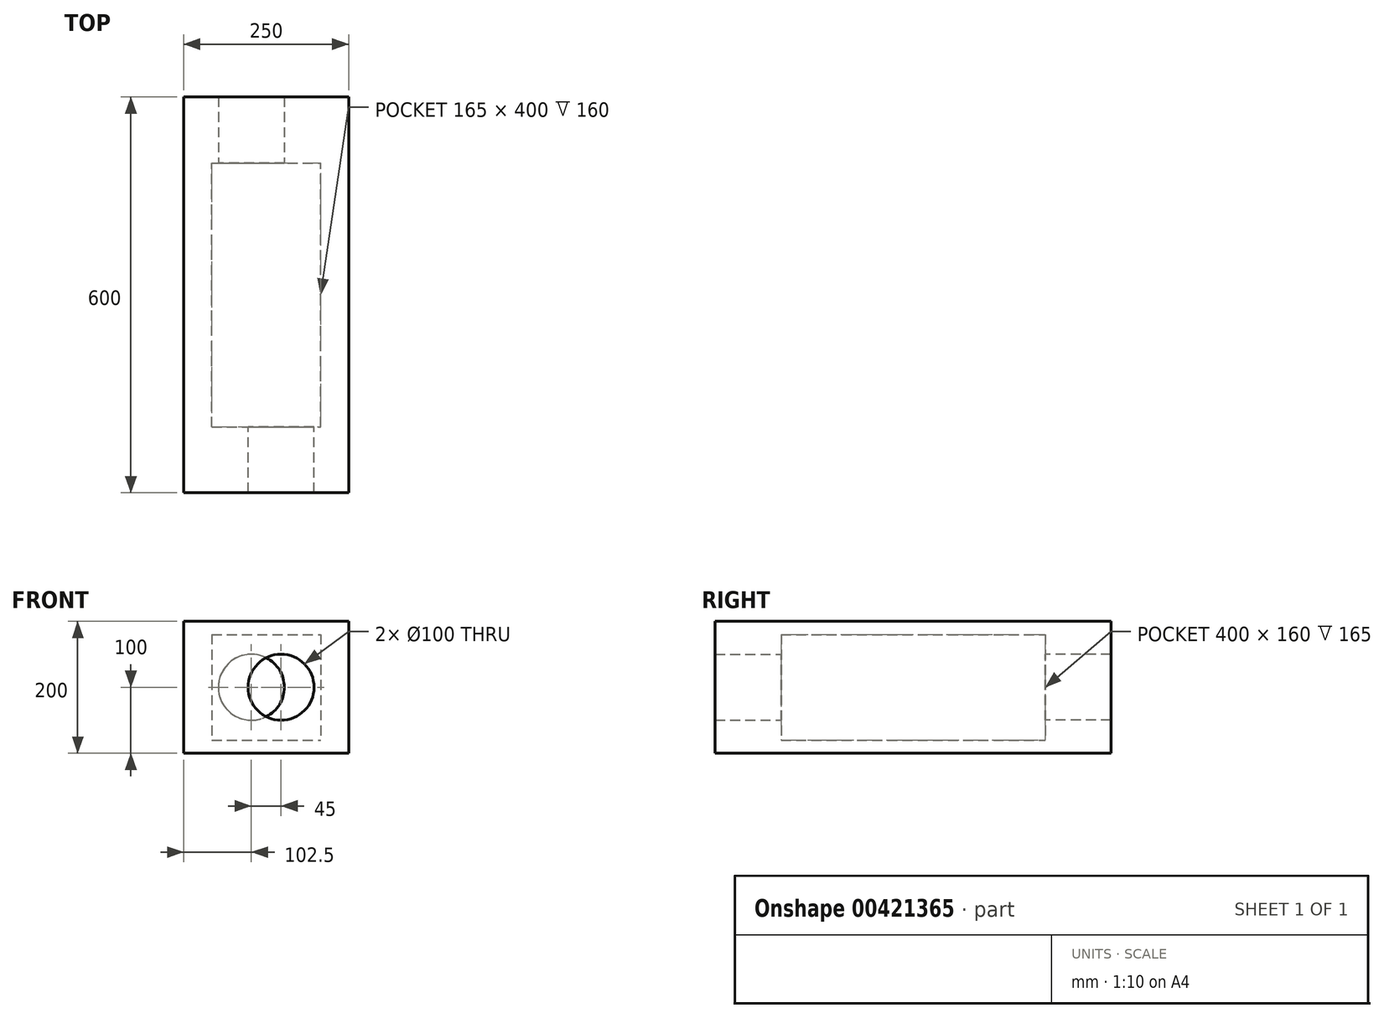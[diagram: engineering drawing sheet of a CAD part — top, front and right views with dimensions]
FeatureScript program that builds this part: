
annotation { "Feature Type Name" : "Feature", "Feature Type Description" : "" }
export const myFeature = defineFeature(function(context is Context, id is Id, definition is map)
    precondition{}
    {
        {
            var Q0;
            Q0=qCreatedBy(makeId("Front.planeOp"),FACE);
            var sketch = newSketch(context, id + "F0", { "sketchPlane" : qUnion([Q0])});
            skCircle(sketch, "E0", {"center": v(0, 0) * mm, "radius": 50 * mm});
            skCircle(sketch, "E1", {"center": v(45, 0) * mm, "radius": 50 * mm});
            skLineSegment(sketch, "E2", {"start": v(0, 0) * mm, "end": v(45, 0) * mm, "construction": true});
            skLineSegment(sketch, "E3.bottom", {"start": v(147.5, 100) * mm, "end": v(-102.5, 100) * mm});
            skLineSegment(sketch, "E3.top", {"start": v(147.5, -100) * mm, "end": v(-102.5, -100) * mm});
            skLineSegment(sketch, "E3.left", {"start": v(147.5, 100) * mm, "end": v(147.5, -100) * mm});
            skLineSegment(sketch, "E3.right", {"start": v(-102.5, 100) * mm, "end": v(-102.5, -100) * mm});
            skPoint(sketch, "E3.middle", {"position": v(22.5, 0) * mm});
            skLineSegment(sketch, "E4.bottom", {"start": v(95, 50) * mm, "end": v(-50, 50) * mm, "construction": true});
            skLineSegment(sketch, "E4.top", {"start": v(95, -50) * mm, "end": v(-50, -50) * mm, "construction": true});
            skLineSegment(sketch, "E4.left", {"start": v(95, 50) * mm, "end": v(95, -50) * mm, "construction": true});
            skLineSegment(sketch, "E4.right", {"start": v(-50, 50) * mm, "end": v(-50, -50) * mm, "construction": true});
            skLineSegment(sketch, "E5.1", {"start": v(105, 80) * mm, "end": v(105, -80) * mm});
            skLineSegment(sketch, "E5.3", {"start": v(-60, 80) * mm, "end": v(-60, -80) * mm});
            skPoint(sketch, "E6", {"position": v(-60, 0) * mm});
            skPoint(sketch, "E7", {"position": v(105, 0) * mm});
            skLineSegment(sketch, "E8", {"start": v(-60, 0) * mm, "end": v(-50, 0) * mm, "construction": true});
            skLineSegment(sketch, "E9", {"start": v(105, 0) * mm, "end": v(95, 0) * mm, "construction": true});
            skLineSegment(sketch, "E10", {"start": v(-60, 80) * mm, "end": v(105, 80) * mm});
            skLineSegment(sketch, "E11", {"start": v(-60, -80) * mm, "end": v(105, -80) * mm});
            skSolve(sketch);
        }
        {
            var Q0;
            Q0=makeQuery(id+"F0.imprint","IMPRINT",FACE,{"disambiguationData":[TD([[makeQuery(id+"F0.imprint","IMPRINT",EDGE,{"derivedFrom":sQuery(id+"F0.wireOp",EDGE,"E3.bottom")}),1.0]])]});
            var Q1;
            Q1=makeQuery(id+"F0.imprint","IMPRINT",FACE,{"disambiguationData":[TD([[makeQuery(id+"F0.imprint","IMPRINT",EDGE,{"derivedFrom":sQuery(id+"F0.wireOp",EDGE,"E5.1")}),-1.0]])]});
            var Q2;
            {var subQ0=sQuery(id+"F0.wireOp",EDGE,"E1");var subQ1=sQuery(id+"F0.wireOp",EDGE,"E0");var subQ2=makeQuery(id+"F0.imprint","INTERSECT",VERTEX,{"disambiguationData":[OD(0.0)],"derivedFrom":[subQ1,subQ0]});Q2=makeQuery(id+"F0.imprint","IMPRINT",FACE,{"disambiguationData":[TD([[makeQuery(id+"F0.imprint","IMPRINT",EDGE,{"disambiguationData":[TD([[subQ2,1.0]])],"derivedFrom":subQ1}),1.0]])]});}
            var Q3;
            {var subQ0=sQuery(id+"F0.wireOp",EDGE,"E1");var subQ1=sQuery(id+"F0.wireOp",EDGE,"E0");var subQ2=makeQuery(id+"F0.imprint","INTERSECT",VERTEX,{"disambiguationData":[OD(0.0)],"derivedFrom":[subQ1,subQ0]});Q3=makeQuery(id+"F0.imprint","IMPRINT",FACE,{"disambiguationData":[TD([[makeQuery(id+"F0.imprint","IMPRINT",EDGE,{"disambiguationData":[TD([[subQ2,-1.0]])],"derivedFrom":subQ1}),1.0]])]});}
            var Q4;
            {var subQ0=sQuery(id+"F0.wireOp",EDGE,"E1");var subQ1=sQuery(id+"F0.wireOp",EDGE,"E0");var subQ2=makeQuery(id+"F0.imprint","INTERSECT",VERTEX,{"disambiguationData":[OD(0.0)],"derivedFrom":[subQ1,subQ0]});Q4=makeQuery(id+"F0.imprint","IMPRINT",FACE,{"disambiguationData":[TD([[makeQuery(id+"F0.imprint","IMPRINT",EDGE,{"disambiguationData":[TD([[subQ2,-1.0]])],"derivedFrom":subQ1}),-1.0]])]});}
            extrude(context, id + "F1", {"entities" : qUnion([Q0, Q1, Q2, Q3, Q4]), "depth" : 300 * mm, "hasSecondDirection" : true, "secondDirectionOppositeDirection" : true, "secondDirectionDepth" : 300 * mm});
        }
        {
            var Q0;
            Q0=makeQuery(id+"F0.imprint","IMPRINT",FACE,{"disambiguationData":[TD([[makeQuery(id+"F0.imprint","IMPRINT",EDGE,{"derivedFrom":sQuery(id+"F0.wireOp",EDGE,"E5.1")}),-1.0]])]});
            var Q1;
            {var subQ0=sQuery(id+"F0.wireOp",EDGE,"E1");var subQ1=sQuery(id+"F0.wireOp",EDGE,"E0");var subQ2=makeQuery(id+"F0.imprint","INTERSECT",VERTEX,{"disambiguationData":[OD(0.0)],"derivedFrom":[subQ1,subQ0]});Q1=makeQuery(id+"F0.imprint","IMPRINT",FACE,{"disambiguationData":[TD([[makeQuery(id+"F0.imprint","IMPRINT",EDGE,{"disambiguationData":[TD([[subQ2,1.0]])],"derivedFrom":subQ1}),1.0]])]});}
            var Q2;
            {var subQ0=sQuery(id+"F0.wireOp",EDGE,"E1");var subQ1=sQuery(id+"F0.wireOp",EDGE,"E0");var subQ2=makeQuery(id+"F0.imprint","INTERSECT",VERTEX,{"disambiguationData":[OD(0.0)],"derivedFrom":[subQ1,subQ0]});Q2=makeQuery(id+"F0.imprint","IMPRINT",FACE,{"disambiguationData":[TD([[makeQuery(id+"F0.imprint","IMPRINT",EDGE,{"disambiguationData":[TD([[subQ2,-1.0]])],"derivedFrom":subQ1}),1.0]])]});}
            var Q3;
            {var subQ0=sQuery(id+"F0.wireOp",EDGE,"E1");var subQ1=sQuery(id+"F0.wireOp",EDGE,"E0");var subQ2=makeQuery(id+"F0.imprint","INTERSECT",VERTEX,{"disambiguationData":[OD(0.0)],"derivedFrom":[subQ1,subQ0]});Q3=makeQuery(id+"F0.imprint","IMPRINT",FACE,{"disambiguationData":[TD([[makeQuery(id+"F0.imprint","IMPRINT",EDGE,{"disambiguationData":[TD([[subQ2,-1.0]])],"derivedFrom":subQ1}),-1.0]])]});}
            extrude(context, id + "F2", {"entities" : qUnion([Q0, Q1, Q2, Q3]), "operationType" : NewBodyOperationType.REMOVE, "depth" : 200 * mm, "hasSecondDirection" : true, "secondDirectionOppositeDirection" : true, "secondDirectionDepth" : 200 * mm});
        }
        {
            var Q0;
            {var subQ0=sQuery(id+"F0.wireOp",EDGE,"E1");var subQ1=sQuery(id+"F0.wireOp",EDGE,"E0");var subQ2=makeQuery(id+"F0.imprint","INTERSECT",VERTEX,{"disambiguationData":[OD(0.0)],"derivedFrom":[subQ1,subQ0]});Q0=makeQuery(id+"F0.imprint","IMPRINT",FACE,{"disambiguationData":[TD([[makeQuery(id+"F0.imprint","IMPRINT",EDGE,{"disambiguationData":[TD([[subQ2,-1.0]])],"derivedFrom":subQ1}),1.0]])]});}
            var Q1;
            {var subQ0=sQuery(id+"F0.wireOp",EDGE,"E1");var subQ1=sQuery(id+"F0.wireOp",EDGE,"E0");var subQ2=makeQuery(id+"F0.imprint","INTERSECT",VERTEX,{"disambiguationData":[OD(0.0)],"derivedFrom":[subQ1,subQ0]});Q1=makeQuery(id+"F0.imprint","IMPRINT",FACE,{"disambiguationData":[TD([[makeQuery(id+"F0.imprint","IMPRINT",EDGE,{"disambiguationData":[TD([[subQ2,-1.0]])],"derivedFrom":subQ1}),-1.0]])]});}
            extrude(context, id + "F3", {"entities" : qUnion([Q0, Q1]), "operationType" : NewBodyOperationType.REMOVE, "endBound" : BoundingType.THROUGH_ALL, "depth" : 25 * mm});
        }
        {
            var Q0;
            {var subQ0=sQuery(id+"F0.wireOp",EDGE,"E1");var subQ1=sQuery(id+"F0.wireOp",EDGE,"E0");var subQ2=makeQuery(id+"F0.imprint","INTERSECT",VERTEX,{"disambiguationData":[OD(0.0)],"derivedFrom":[subQ1,subQ0]});Q0=makeQuery(id+"F0.imprint","IMPRINT",FACE,{"disambiguationData":[TD([[makeQuery(id+"F0.imprint","IMPRINT",EDGE,{"disambiguationData":[TD([[subQ2,1.0]])],"derivedFrom":subQ1}),1.0]])]});}
            var Q1;
            {var subQ0=sQuery(id+"F0.wireOp",EDGE,"E1");var subQ1=sQuery(id+"F0.wireOp",EDGE,"E0");var subQ2=makeQuery(id+"F0.imprint","INTERSECT",VERTEX,{"disambiguationData":[OD(0.0)],"derivedFrom":[subQ1,subQ0]});Q1=makeQuery(id+"F0.imprint","IMPRINT",FACE,{"disambiguationData":[TD([[makeQuery(id+"F0.imprint","IMPRINT",EDGE,{"disambiguationData":[TD([[subQ2,-1.0]])],"derivedFrom":subQ1}),1.0]])]});}
            extrude(context, id + "F4", {"entities" : qUnion([Q0, Q1]), "operationType" : NewBodyOperationType.REMOVE, "endBound" : BoundingType.THROUGH_ALL, "oppositeDirection" : true, "depth" : 25 * mm});
        }
    });
